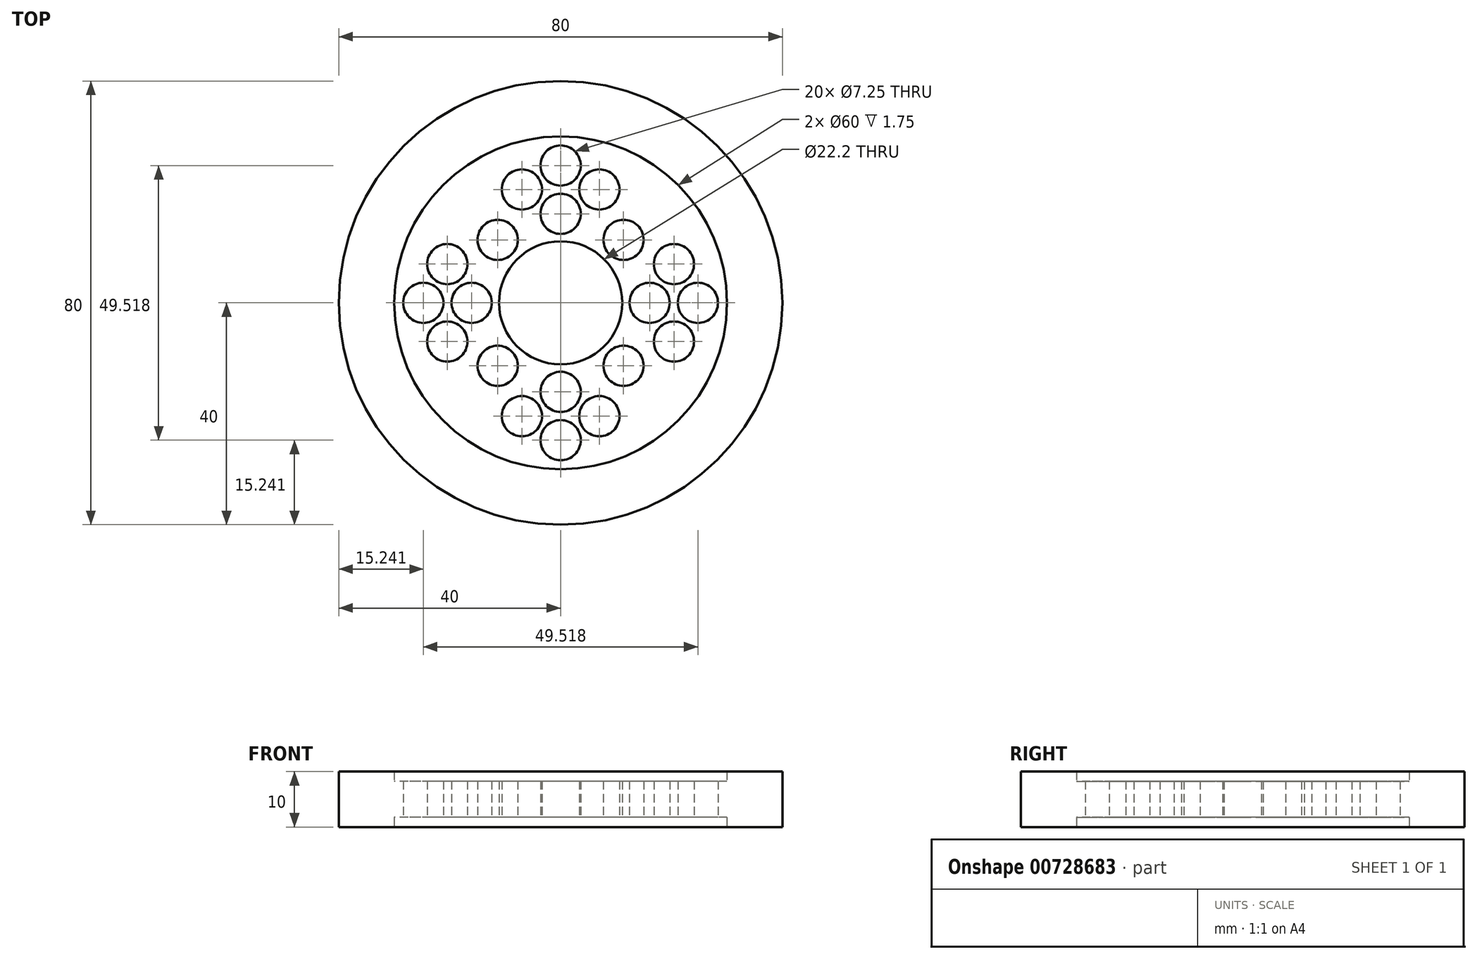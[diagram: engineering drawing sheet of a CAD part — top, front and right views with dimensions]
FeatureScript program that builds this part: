
annotation { "Feature Type Name" : "Feature", "Feature Type Description" : "" }
export const myFeature = defineFeature(function(context is Context, id is Id, definition is map)
    precondition{}
    {
        {
            var Q0;
            Q0=qCreatedBy(makeId("Top.planeOp"),FACE);
            var sketch = newSketch(context, id + "F0", { "sketchPlane" : qUnion([Q0])});
            skCircle(sketch, "E0", {"center": v(0, 0) * mm, "radius": 11.1 * mm});
            skCircle(sketch, "E1", {"center": v(0, 0) * mm, "radius": 30 * mm});
            skCircle(sketch, "E2", {"center": v(-16.05, 0) * mm, "radius": 3.62 * mm});
            skCircle(sketch, "E3", {"center": v(-24.76, 0) * mm, "radius": 3.62 * mm});
            skCircle(sketch, "E4.1.0", {"center": v(0, -24.76) * mm, "radius": 3.62 * mm});
            skCircle(sketch, "E4.1.1", {"center": v(0, -16.05) * mm, "radius": 3.62 * mm});
            skCircle(sketch, "E4.2.0", {"center": v(24.76, 0) * mm, "radius": 3.62 * mm});
            skCircle(sketch, "E4.2.1", {"center": v(16.05, 0) * mm, "radius": 3.62 * mm});
            skCircle(sketch, "E4.3.0", {"center": v(0, 24.76) * mm, "radius": 3.62 * mm});
            skCircle(sketch, "E4.3.1", {"center": v(0, 16.05) * mm, "radius": 3.62 * mm});
            skCircle(sketch, "E5", {"center": v(-20.44, 6.98) * mm, "radius": 3.62 * mm});
            skCircle(sketch, "E6.MirrorC", {"center": v(-20.44, -6.98) * mm, "radius": 3.62 * mm});
            skCircle(sketch, "E7.1.0", {"center": v(-6.98, -20.44) * mm, "radius": 3.62 * mm});
            skCircle(sketch, "E7.1.1", {"center": v(6.98, -20.44) * mm, "radius": 3.62 * mm});
            skCircle(sketch, "E7.2.0", {"center": v(20.44, -6.98) * mm, "radius": 3.62 * mm});
            skCircle(sketch, "E7.2.1", {"center": v(20.44, 6.98) * mm, "radius": 3.62 * mm});
            skCircle(sketch, "E7.3.0", {"center": v(6.98, 20.44) * mm, "radius": 3.62 * mm});
            skCircle(sketch, "E7.3.1", {"center": v(-6.98, 20.44) * mm, "radius": 3.62 * mm});
            skCircle(sketch, "E8.1.0", {"center": v(-11.35, -11.35) * mm, "radius": 3.62 * mm});
            skCircle(sketch, "E8.3.0", {"center": v(11.35, -11.35) * mm, "radius": 3.62 * mm});
            skCircle(sketch, "E8.5.0", {"center": v(11.35, 11.35) * mm, "radius": 3.62 * mm});
            skCircle(sketch, "E8.7.0", {"center": v(-11.35, 11.35) * mm, "radius": 3.62 * mm});
            skSolve(sketch);
        }
        {
            var Q0;
            Q0=qCreatedBy(makeId("Top.planeOp"),FACE);
            var sketch = newSketch(context, id + "F1", { "sketchPlane" : qUnion([Q0])});
            skCircle(sketch, "E9", {"center": v(0, 0) * mm, "radius": 30 * mm});
            skCircle(sketch, "E10", {"center": v(0, 0) * mm, "radius": 40 * mm});
            skSolve(sketch);
        }
        {
            var Q0;
            Q0=makeQuery(id+"F0.imprint","IMPRINT",FACE,{"disambiguationData":[TD([[makeQuery(id+"F0.imprint","IMPRINT",EDGE,{"derivedFrom":sQuery(id+"F0.wireOp",EDGE,"E0")}),-1.0]])]});
            extrude(context, id + "F2", {"entities" : qUnion([Q0]), "depth" : 3.25 * mm, "offsetDistance" : 25 * mm, "hasSecondDirection" : true, "secondDirectionOppositeDirection" : true, "secondDirectionDepth" : 3.25 * mm});
        }
        {
            var Q0;
            Q0 = qSketchRegion(id + "F1", true);
            extrude(context, id + "F3", {"entities" : qUnion([Q0]), "operationType" : NewBodyOperationType.ADD, "depth" : 5 * mm, "offsetDistance" : 25 * mm, "hasSecondDirection" : true, "secondDirectionOppositeDirection" : true, "secondDirectionDepth" : 5 * mm});
        }
    });
